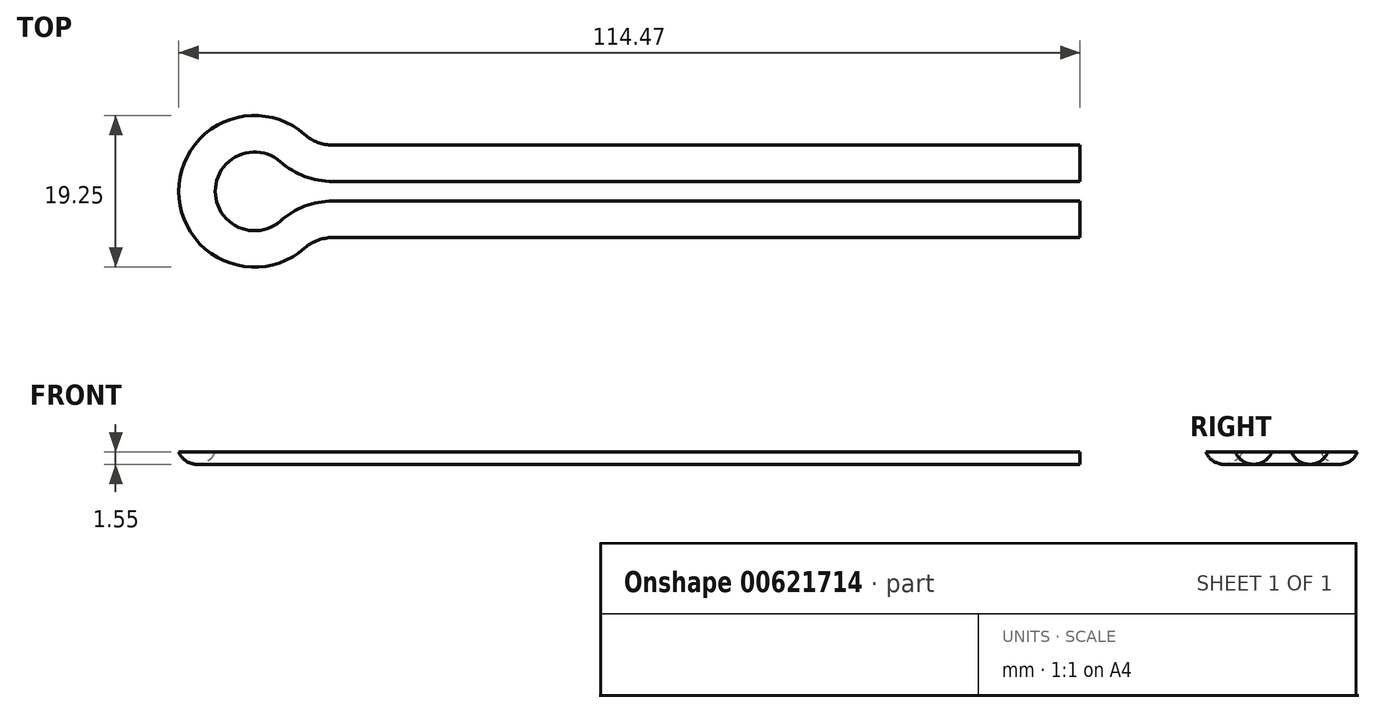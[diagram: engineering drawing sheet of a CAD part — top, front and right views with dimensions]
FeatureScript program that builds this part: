
annotation { "Feature Type Name" : "Feature", "Feature Type Description" : "" }
export const myFeature = defineFeature(function(context is Context, id is Id, definition is map)
    precondition{}
    {
        {
            var Q0;
            Q0=qCreatedBy(makeId("Top.planeOp"),FACE);
            var sketch = newSketch(context, id + "F0", { "sketchPlane" : qUnion([Q0])});
            skLineSegment(sketch, "E0", {"start": v(67.85, 27.15) * mm, "end": v(-27.07, 27.15) * mm});
            skLineSegment(sketch, "E1", {"start": v(67.85, 24.65) * mm, "end": v(-27.07, 24.65) * mm});
            skArc(sketch, "E2", {"start": v(-33.69, 29.65) * mm, "mid": v(-42, 25.9) * mm, "end": v(-33.69, 22.15) * mm});
            skPoint(sketch, "E3.visualSharp", {"position": v(-32.15, 27.15) * mm});
            skArc(sketch, "E3.filletArc", {"start": v(-33.69, 29.65) * mm, "mid": v(-30.6, 27.8) * mm, "end": v(-27.07, 27.15) * mm});
            skPoint(sketch, "E4.visualSharp", {"position": v(-32.15, 24.65) * mm});
            skArc(sketch, "E4.filletArc", {"start": v(-27.07, 24.65) * mm, "mid": v(-30.6, 24) * mm, "end": v(-33.69, 22.15) * mm});
            skSolve(sketch);
        }
        {
            var Q0;
            Q0=sQuery(id+"F0.wireOp",VERTEX,"E1.start");
            var Q1;
            Q1=qCreatedBy(makeId("Right.planeOp"),FACE);
            cPlane(context, id + "F1", {"entities" : qUnion([Q0, Q1]), "cplaneType" : CPlaneType.PLANE_POINT, "offset" : 25 * mm, "width" : 150 * mm, "height" : 150 * mm});
        }
        {
            var Q0;
            Q0=qCreatedBy(id+"F1.planeOp",FACE);
            var sketch = newSketch(context, id + "F2", { "sketchPlane" : qUnion([Q0])});
            skArc(sketch, "E5", {"start": v(20.02, 0) * mm, "mid": v(22.34, -1.55) * mm, "end": v(24.65, 0) * mm});
            skLineSegment(sketch, "E6", {"start": v(24.65, 0) * mm, "end": v(20.02, 0) * mm});
            skSolve(sketch);
        }
        {
            var Q0;
            Q0 = qSketchRegion(id + "F2", true);
            var Q1;
            Q1 = qConstructionFilter(qBodyType(qCreatedBy(id + "F0" ,EDGE), BodyType.WIRE), ConstructionObject.NO);
            sweep(context, id + "F3", {"profiles" : qUnion([Q0]), "path" : qUnion([Q1])});
        }
    });
